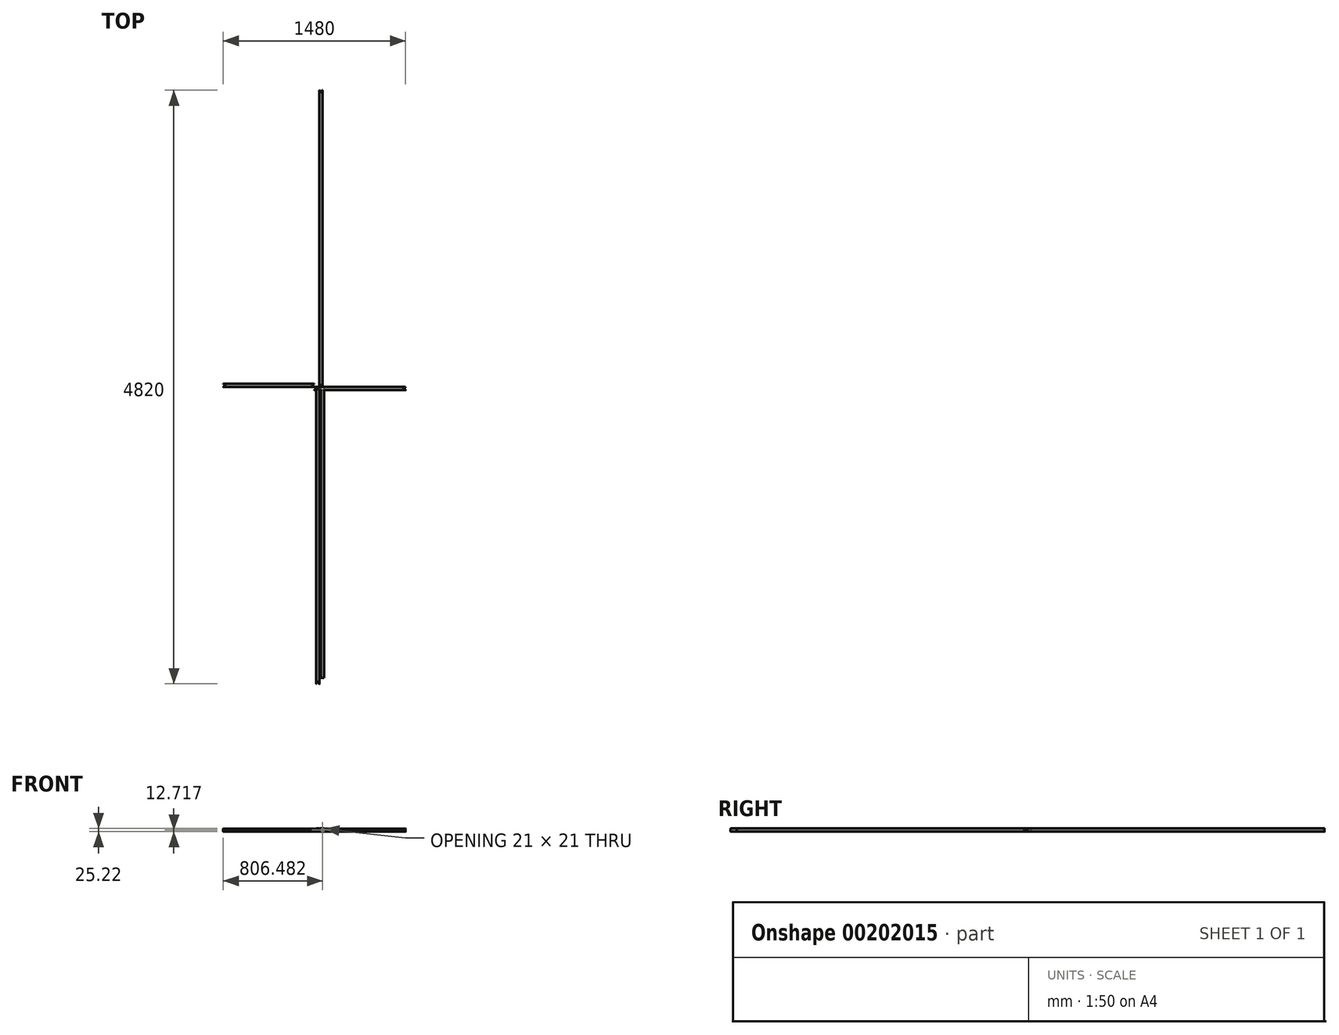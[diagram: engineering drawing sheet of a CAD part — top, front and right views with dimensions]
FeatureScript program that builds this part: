
annotation { "Feature Type Name" : "Feature", "Feature Type Description" : "" }
export const myFeature = defineFeature(function(context is Context, id is Id, definition is map)
    precondition{}
    {
        {
            var Q0;
            Q0=qCreatedBy(makeId("Front.planeOp"),FACE);
            var sketch = newSketch(context, id + "F0", { "sketchPlane" : qUnion([Q0])});
            skLineSegment(sketch, "E0.bottom", {"start": v(10, 12.5) * mm, "end": v(-10, 12.5) * mm});
            skLineSegment(sketch, "E0.top", {"start": v(10, -12.5) * mm, "end": v(-10, -12.5) * mm});
            skLineSegment(sketch, "E0.left", {"start": v(12.5, 10) * mm, "end": v(12.5, -10) * mm});
            skLineSegment(sketch, "E0.right", {"start": v(-12.5, 10) * mm, "end": v(-12.5, -10) * mm});
            skPoint(sketch, "E0.middle", {"position": v(0, 0) * mm});
            skLineSegment(sketch, "E1.0", {"start": v(8.5, 10.5) * mm, "end": v(-8.5, 10.5) * mm});
            skLineSegment(sketch, "E1.1", {"start": v(10.5, 8.5) * mm, "end": v(10.5, -8.5) * mm});
            skLineSegment(sketch, "E1.2", {"start": v(8.5, -10.5) * mm, "end": v(-8.5, -10.5) * mm});
            skLineSegment(sketch, "E1.3", {"start": v(-10.5, 8.5) * mm, "end": v(-10.5, -8.5) * mm});
            skPoint(sketch, "E2.visualSharp", {"position": v(-10.5, 10.5) * mm});
            skArc(sketch, "E2.filletArc", {"start": v(-8.5, 10.5) * mm, "mid": v(-9.91, 9.91) * mm, "end": v(-10.5, 8.5) * mm});
            skPoint(sketch, "E3.visualSharp", {"position": v(10.5, 10.5) * mm});
            skArc(sketch, "E3.filletArc", {"start": v(10.5, 8.5) * mm, "mid": v(9.91, 9.91) * mm, "end": v(8.5, 10.5) * mm});
            skPoint(sketch, "E4.visualSharp", {"position": v(10.5, -10.5) * mm});
            skArc(sketch, "E4.filletArc", {"start": v(8.5, -10.5) * mm, "mid": v(9.91, -9.91) * mm, "end": v(10.5, -8.5) * mm});
            skPoint(sketch, "E5.visualSharp", {"position": v(-10.5, -10.5) * mm});
            skArc(sketch, "E5.filletArc", {"start": v(-10.5, -8.5) * mm, "mid": v(-9.91, -9.91) * mm, "end": v(-8.5, -10.5) * mm});
            skPoint(sketch, "E6.visualSharp", {"position": v(12.5, 12.5) * mm});
            skArc(sketch, "E6.filletArc", {"start": v(12.5, 10) * mm, "mid": v(11.77, 11.77) * mm, "end": v(10, 12.5) * mm});
            skPoint(sketch, "E7.visualSharp", {"position": v(-12.5, 12.5) * mm});
            skArc(sketch, "E7.filletArc", {"start": v(-10, 12.5) * mm, "mid": v(-11.77, 11.77) * mm, "end": v(-12.5, 10) * mm});
            skPoint(sketch, "E8.visualSharp", {"position": v(12.5, -12.5) * mm});
            skArc(sketch, "E8.filletArc", {"start": v(10, -12.5) * mm, "mid": v(11.77, -11.77) * mm, "end": v(12.5, -10) * mm});
            skPoint(sketch, "E9.visualSharp", {"position": v(-12.5, -12.5) * mm});
            skArc(sketch, "E9.filletArc", {"start": v(-12.5, -10) * mm, "mid": v(-11.77, -11.77) * mm, "end": v(-10, -12.5) * mm});
            skSolve(sketch);
        }
        {
            var Q0;
            Q0=makeQuery(id+"F0.imprint","IMPRINT",FACE,{"disambiguationData":[TD([[makeQuery(id+"F0.imprint","IMPRINT",EDGE,{"derivedFrom":sQuery(id+"F0.wireOp",EDGE,"E0.bottom")}),1.0]])]});
            extrude(context, id + "F1", {"entities" : qUnion([Q0]), "depth" : 2410 * mm});
        }
        {
            var Q0;
            Q0=makeQuery(id+"F1.opExtrude","SWEPT_FACE",FACE,{"disambiguationData":[OSD([sQuery(id+"F0.wireOp",EDGE,"E0.bottom")])]});
            var sketch = newSketch(context, id + "F2", { "sketchPlane" : qUnion([Q0])});
            skLineSegment(sketch, "E10.0", {"start": v(-12.5, -2410) * mm, "end": v(-12.5, 0) * mm});
            skLineSegment(sketch, "E11.0", {"start": v(12.5, -2410) * mm, "end": v(12.5, 0) * mm});
            skLineSegment(sketch, "E12", {"start": v(-12.5, 0) * mm, "end": v(12.5, 0) * mm});
            skLineSegment(sketch, "E13", {"start": v(12.5, 0) * mm, "end": v(-12.5, -25) * mm});
            skLineSegment(sketch, "E14", {"start": v(-12.5, -25) * mm, "end": v(-12.5, 0) * mm});
            skLineSegment(sketch, "E15", {"start": v(12.5, -2410) * mm, "end": v(-12.5, -2385) * mm});
            skLineSegment(sketch, "E16", {"start": v(-12.5, -2385) * mm, "end": v(-12.5, -2410) * mm});
            skLineSegment(sketch, "E17", {"start": v(-12.5, -2410) * mm, "end": v(12.5, -2410) * mm});
            skSolve(sketch);
        }
        {
            var Q0;
            {var subQ0=sQuery(id+"F2.wireOp",EDGE,"E12");var subQ1=sQuery(id+"F0.wireOp",EDGE,"E0.bottom");var subQ2=makeQuery(id+"F1.opExtrude","SWEPT_EDGE",EDGE,{"disambiguationData":[OSD([subQ1,sQuery(id+"F0.wireOp",EDGE,"E6.filletArc")])]});var subQ3=makeQuery(id+"F2.imprint","INTERSECT",VERTEX,{"derivedFrom":[subQ2,subQ0]});var subQ4=makeQuery(id+"F1.opExtrude","SWEPT_EDGE",EDGE,{"disambiguationData":[OSD([subQ1,sQuery(id+"F0.wireOp",EDGE,"E7.filletArc")])]});var subQ5=makeQuery(id+"F2.imprint","INTERSECT",VERTEX,{"derivedFrom":[subQ4,subQ0]});Q0=makeQuery(id+"F2.imprint","IMPRINT",FACE,{"disambiguationData":[TD([[makeQuery(id+"F2.imprint","IMPRINT",EDGE,{"disambiguationData":[TD([[subQ3,-1.0],[subQ5,1.0]])],"derivedFrom":subQ0}),1.0]])]});}
            var Q1;
            {var subQ3=sQuery(id+"F2.wireOp",EDGE,"E14");Q1=makeQuery(id+"F2.imprint","IMPRINT",FACE,{"disambiguationData":[TD([[makeQuery(id+"F2.imprint","IMPRINT",EDGE,{"derivedFrom":subQ3}),-1.0]])]});}
            var Q2;
            {var subQ0=sQuery(id+"F2.wireOp",EDGE,"E12");var subQ1=makeQuery(id+"F1.opExtrude","SWEPT_EDGE",EDGE,{"disambiguationData":[OSD([sQuery(id+"F0.wireOp",EDGE,"E0.bottom"),sQuery(id+"F0.wireOp",EDGE,"E6.filletArc")])]});var subQ2=makeQuery(id+"F2.imprint","INTERSECT",VERTEX,{"derivedFrom":[subQ1,subQ0]});var subQ3=sQuery(id+"F2.wireOp",EDGE,"E13");var subQ4=makeQuery(id+"F2.imprint","INTERSECT",VERTEX,{"derivedFrom":[subQ0,subQ3]});Q2=makeQuery(id+"F2.imprint","IMPRINT",FACE,{"disambiguationData":[TD([[makeQuery(id+"F2.imprint","IMPRINT",EDGE,{"disambiguationData":[TD([[subQ2,-1.0],[subQ4,1.0]])],"derivedFrom":subQ0}),-1.0]])]});}
            var Q3;
            {var subQ0=sQuery(id+"F2.wireOp",EDGE,"E15");var subQ1=sQuery(id+"F0.wireOp",EDGE,"E0.bottom");var subQ2=makeQuery(id+"F1.opExtrude","SWEPT_EDGE",EDGE,{"disambiguationData":[OSD([subQ1,sQuery(id+"F0.wireOp",EDGE,"E6.filletArc")])]});var subQ3=makeQuery(id+"F2.imprint","INTERSECT",VERTEX,{"derivedFrom":[subQ2,subQ0]});Q3=makeQuery(id+"F2.imprint","IMPRINT",FACE,{"disambiguationData":[TD([[makeQuery(id+"F2.imprint","IMPRINT",EDGE,{"disambiguationData":[TD([[subQ3,-1.0]])],"derivedFrom":subQ0}),1.0]])]});}
            var Q4;
            {var subQ0=sQuery(id+"F2.wireOp",EDGE,"E16");Q4=makeQuery(id+"F2.imprint","IMPRINT",FACE,{"disambiguationData":[TD([[makeQuery(id+"F2.imprint","IMPRINT",EDGE,{"derivedFrom":subQ0}),1.0]])]});}
            var Q5;
            {var subQ0=sQuery(id+"F2.wireOp",EDGE,"E17");var subQ1=sQuery(id+"F2.wireOp",EDGE,"E15");var subQ2=makeQuery(id+"F2.imprint","INTERSECT",VERTEX,{"derivedFrom":[sQuery(id+"F2.wireOp",EDGE,"E11.0"),subQ1,subQ0]});Q5=makeQuery(id+"F2.imprint","IMPRINT",FACE,{"disambiguationData":[TD([[makeQuery(id+"F2.imprint","IMPRINT",EDGE,{"disambiguationData":[TD([[subQ2,-1.0]])],"derivedFrom":subQ1}),1.0]])]});}
            extrude(context, id + "F3", {"entities" : qUnion([Q0, Q1, Q2, Q3, Q4, Q5]), "operationType" : NewBodyOperationType.REMOVE, "endBound" : BoundingType.THROUGH_ALL, "oppositeDirection" : true, "depth" : 25 * mm});
        }
        {
            var Q0;
            Q0=qCreatedBy(makeId("Front.planeOp"),FACE);
            var sketch = newSketch(context, id + "F4", { "sketchPlane" : qUnion([Q0])});
            skLineSegment(sketch, "E18.bottom", {"start": v(-30.64, 12.45) * mm, "end": v(-50.64, 12.45) * mm});
            skLineSegment(sketch, "E18.top", {"start": v(-30.64, -12.55) * mm, "end": v(-50.64, -12.55) * mm});
            skLineSegment(sketch, "E18.left", {"start": v(-28.14, 9.95) * mm, "end": v(-28.14, -10.05) * mm});
            skLineSegment(sketch, "E18.right", {"start": v(-53.14, 9.95) * mm, "end": v(-53.14, -10.05) * mm});
            skPoint(sketch, "E18.middle", {"position": v(-40.64, -0.05) * mm});
            skLineSegment(sketch, "E19.0", {"start": v(-32.14, 10.45) * mm, "end": v(-49.14, 10.45) * mm});
            skLineSegment(sketch, "E19.1", {"start": v(-30.14, 8.45) * mm, "end": v(-30.14, -8.55) * mm});
            skLineSegment(sketch, "E19.2", {"start": v(-32.14, -10.55) * mm, "end": v(-49.14, -10.55) * mm});
            skLineSegment(sketch, "E19.3", {"start": v(-51.14, 8.45) * mm, "end": v(-51.14, -8.55) * mm});
            skPoint(sketch, "E20.visualSharp", {"position": v(-51.14, 10.45) * mm});
            skArc(sketch, "E20.filletArc", {"start": v(-49.14, 10.45) * mm, "mid": v(-50.56, 9.86) * mm, "end": v(-51.14, 8.45) * mm});
            skPoint(sketch, "E21.visualSharp", {"position": v(-30.14, 10.45) * mm});
            skArc(sketch, "E21.filletArc", {"start": v(-30.14, 8.45) * mm, "mid": v(-30.73, 9.86) * mm, "end": v(-32.14, 10.45) * mm});
            skPoint(sketch, "E22.visualSharp", {"position": v(-30.14, -10.55) * mm});
            skArc(sketch, "E22.filletArc", {"start": v(-32.14, -10.55) * mm, "mid": v(-30.73, -9.96) * mm, "end": v(-30.14, -8.55) * mm});
            skPoint(sketch, "E23.visualSharp", {"position": v(-51.14, -10.55) * mm});
            skArc(sketch, "E23.filletArc", {"start": v(-51.14, -8.55) * mm, "mid": v(-50.56, -9.96) * mm, "end": v(-49.14, -10.55) * mm});
            skPoint(sketch, "E24.visualSharp", {"position": v(-28.14, 12.45) * mm});
            skArc(sketch, "E24.filletArc", {"start": v(-28.14, 9.95) * mm, "mid": v(-28.87, 11.72) * mm, "end": v(-30.64, 12.45) * mm});
            skPoint(sketch, "E25.visualSharp", {"position": v(-53.14, 12.45) * mm});
            skArc(sketch, "E25.filletArc", {"start": v(-50.64, 12.45) * mm, "mid": v(-52.4, 11.72) * mm, "end": v(-53.14, 9.95) * mm});
            skPoint(sketch, "E26.visualSharp", {"position": v(-28.14, -12.55) * mm});
            skArc(sketch, "E26.filletArc", {"start": v(-30.64, -12.55) * mm, "mid": v(-28.87, -11.82) * mm, "end": v(-28.14, -10.05) * mm});
            skPoint(sketch, "E27.visualSharp", {"position": v(-53.14, -12.55) * mm});
            skArc(sketch, "E27.filletArc", {"start": v(-53.14, -10.05) * mm, "mid": v(-52.4, -11.82) * mm, "end": v(-50.64, -12.55) * mm});
            skSolve(sketch);
        }
        {
            var Q0;
            Q0=makeQuery(id+"F4.imprint","IMPRINT",FACE,{"disambiguationData":[TD([[makeQuery(id+"F4.imprint","IMPRINT",EDGE,{"derivedFrom":sQuery(id+"F4.wireOp",EDGE,"E18.bottom")}),1.0]])]});
            extrude(context, id + "F5", {"entities" : qUnion([Q0]), "depth" : 740 * mm});
        }
        {
            var Q0;
            Q0=makeQuery(id+"F5.opExtrude","SWEPT_FACE",FACE,{"disambiguationData":[OSD([sQuery(id+"F4.wireOp",EDGE,"E18.bottom")])]});
            var sketch = newSketch(context, id + "F6", { "sketchPlane" : qUnion([Q0])});
            skLineSegment(sketch, "E28.0", {"start": v(-28.14, -740) * mm, "end": v(-28.14, 0) * mm});
            skLineSegment(sketch, "E29.0", {"start": v(-53.14, -740) * mm, "end": v(-53.14, 0) * mm});
            skLineSegment(sketch, "E30", {"start": v(-53.14, 0) * mm, "end": v(-28.14, 0) * mm});
            skLineSegment(sketch, "E31", {"start": v(-28.14, 0) * mm, "end": v(-53.14, -25) * mm});
            skLineSegment(sketch, "E32", {"start": v(-53.14, -25) * mm, "end": v(-53.14, 0) * mm});
            skLineSegment(sketch, "E33", {"start": v(-28.14, -740) * mm, "end": v(-53.14, -715) * mm});
            skLineSegment(sketch, "E34", {"start": v(-53.14, -715) * mm, "end": v(-53.14, -740) * mm});
            skLineSegment(sketch, "E35", {"start": v(-53.14, -740) * mm, "end": v(-28.14, -740) * mm});
            skSolve(sketch);
        }
        {
            var Q0;
            {var subQ0=sQuery(id+"F6.wireOp",EDGE,"E34");Q0=makeQuery(id+"F6.imprint","IMPRINT",FACE,{"disambiguationData":[TD([[makeQuery(id+"F6.imprint","IMPRINT",EDGE,{"derivedFrom":subQ0}),1.0]])]});}
            var Q1;
            {var subQ0=sQuery(id+"F6.wireOp",EDGE,"E33");var subQ1=sQuery(id+"F4.wireOp",EDGE,"E18.bottom");var subQ2=makeQuery(id+"F5.opExtrude","SWEPT_EDGE",EDGE,{"disambiguationData":[OSD([subQ1,sQuery(id+"F4.wireOp",EDGE,"E24.filletArc")])]});var subQ3=makeQuery(id+"F6.imprint","INTERSECT",VERTEX,{"derivedFrom":[subQ2,subQ0]});Q1=makeQuery(id+"F6.imprint","IMPRINT",FACE,{"disambiguationData":[TD([[makeQuery(id+"F6.imprint","IMPRINT",EDGE,{"disambiguationData":[TD([[subQ3,-1.0]])],"derivedFrom":subQ0}),1.0]])]});}
            var Q2;
            {var subQ0=sQuery(id+"F6.wireOp",EDGE,"E35");var subQ1=sQuery(id+"F6.wireOp",EDGE,"E33");var subQ2=makeQuery(id+"F6.imprint","INTERSECT",VERTEX,{"derivedFrom":[sQuery(id+"F6.wireOp",EDGE,"E28.0"),subQ1,subQ0]});Q2=makeQuery(id+"F6.imprint","IMPRINT",FACE,{"disambiguationData":[TD([[makeQuery(id+"F6.imprint","IMPRINT",EDGE,{"disambiguationData":[TD([[subQ2,-1.0]])],"derivedFrom":subQ1}),1.0]])]});}
            var Q3;
            {var subQ3=sQuery(id+"F6.wireOp",EDGE,"E32");Q3=makeQuery(id+"F6.imprint","IMPRINT",FACE,{"disambiguationData":[TD([[makeQuery(id+"F6.imprint","IMPRINT",EDGE,{"derivedFrom":subQ3}),-1.0]])]});}
            var Q4;
            {var subQ0=sQuery(id+"F6.wireOp",EDGE,"E30");var subQ1=sQuery(id+"F4.wireOp",EDGE,"E18.bottom");var subQ2=makeQuery(id+"F5.opExtrude","SWEPT_EDGE",EDGE,{"disambiguationData":[OSD([subQ1,sQuery(id+"F4.wireOp",EDGE,"E24.filletArc")])]});var subQ3=makeQuery(id+"F6.imprint","INTERSECT",VERTEX,{"derivedFrom":[subQ2,subQ0]});var subQ4=makeQuery(id+"F5.opExtrude","SWEPT_EDGE",EDGE,{"disambiguationData":[OSD([subQ1,sQuery(id+"F4.wireOp",EDGE,"E25.filletArc")])]});var subQ5=makeQuery(id+"F6.imprint","INTERSECT",VERTEX,{"derivedFrom":[subQ4,subQ0]});Q4=makeQuery(id+"F6.imprint","IMPRINT",FACE,{"disambiguationData":[TD([[makeQuery(id+"F6.imprint","IMPRINT",EDGE,{"disambiguationData":[TD([[subQ3,-1.0],[subQ5,1.0]])],"derivedFrom":subQ0}),1.0]])]});}
            var Q5;
            {var subQ0=sQuery(id+"F6.wireOp",EDGE,"E30");var subQ1=makeQuery(id+"F5.opExtrude","SWEPT_EDGE",EDGE,{"disambiguationData":[OSD([sQuery(id+"F4.wireOp",EDGE,"E18.bottom"),sQuery(id+"F4.wireOp",EDGE,"E24.filletArc")])]});var subQ2=makeQuery(id+"F6.imprint","INTERSECT",VERTEX,{"derivedFrom":[subQ1,subQ0]});var subQ3=sQuery(id+"F6.wireOp",EDGE,"E31");var subQ4=makeQuery(id+"F6.imprint","INTERSECT",VERTEX,{"derivedFrom":[sQuery(id+"F6.wireOp",EDGE,"E28.0"),subQ0,subQ3]});Q5=makeQuery(id+"F6.imprint","IMPRINT",FACE,{"disambiguationData":[TD([[makeQuery(id+"F6.imprint","IMPRINT",EDGE,{"disambiguationData":[TD([[subQ2,-1.0],[subQ4,1.0]])],"derivedFrom":subQ0}),-1.0]])]});}
            extrude(context, id + "F7", {"entities" : qUnion([Q0, Q1, Q2, Q3, Q4, Q5]), "operationType" : NewBodyOperationType.REMOVE, "oppositeDirection" : true, "depth" : 25 * mm});
        }
        {
            var Q0;
            Q0=qCreatedBy(makeId("Front.planeOp"),FACE);
            var sketch = newSketch(context, id + "F8", { "sketchPlane" : qUnion([Q0])});
            skLineSegment(sketch, "E36.bottom", {"start": v(48.34, 12.67) * mm, "end": v(28.34, 12.67) * mm});
            skLineSegment(sketch, "E36.top", {"start": v(48.34, -12.33) * mm, "end": v(28.34, -12.33) * mm});
            skLineSegment(sketch, "E36.left", {"start": v(50.84, 10.17) * mm, "end": v(50.84, -9.83) * mm});
            skLineSegment(sketch, "E36.right", {"start": v(25.84, 10.17) * mm, "end": v(25.84, -9.83) * mm});
            skPoint(sketch, "E36.middle", {"position": v(38.34, 0.17) * mm});
            skLineSegment(sketch, "E37.0", {"start": v(46.84, 10.67) * mm, "end": v(29.84, 10.67) * mm});
            skLineSegment(sketch, "E37.1", {"start": v(48.84, 8.67) * mm, "end": v(48.84, -8.33) * mm});
            skLineSegment(sketch, "E37.2", {"start": v(46.84, -10.33) * mm, "end": v(29.84, -10.33) * mm});
            skLineSegment(sketch, "E37.3", {"start": v(27.84, 8.67) * mm, "end": v(27.84, -8.33) * mm});
            skPoint(sketch, "E38.visualSharp", {"position": v(27.84, 10.67) * mm});
            skArc(sketch, "E38.filletArc", {"start": v(29.84, 10.67) * mm, "mid": v(28.43, 10.08) * mm, "end": v(27.84, 8.67) * mm});
            skPoint(sketch, "E39.visualSharp", {"position": v(48.84, 10.67) * mm});
            skArc(sketch, "E39.filletArc", {"start": v(48.84, 8.67) * mm, "mid": v(48.26, 10.08) * mm, "end": v(46.84, 10.67) * mm});
            skPoint(sketch, "E40.visualSharp", {"position": v(48.84, -10.33) * mm});
            skArc(sketch, "E40.filletArc", {"start": v(46.84, -10.33) * mm, "mid": v(48.26, -9.75) * mm, "end": v(48.84, -8.33) * mm});
            skPoint(sketch, "E41.visualSharp", {"position": v(27.84, -10.33) * mm});
            skArc(sketch, "E41.filletArc", {"start": v(27.84, -8.33) * mm, "mid": v(28.43, -9.75) * mm, "end": v(29.84, -10.33) * mm});
            skPoint(sketch, "E42.visualSharp", {"position": v(50.84, 12.67) * mm});
            skArc(sketch, "E42.filletArc", {"start": v(50.84, 10.17) * mm, "mid": v(50.1, 11.93) * mm, "end": v(48.34, 12.67) * mm});
            skPoint(sketch, "E43.visualSharp", {"position": v(25.84, 12.67) * mm});
            skArc(sketch, "E43.filletArc", {"start": v(28.34, 12.67) * mm, "mid": v(26.57, 11.93) * mm, "end": v(25.84, 10.17) * mm});
            skPoint(sketch, "E44.visualSharp", {"position": v(50.84, -12.33) * mm});
            skArc(sketch, "E44.filletArc", {"start": v(48.34, -12.33) * mm, "mid": v(50.1, -11.6) * mm, "end": v(50.84, -9.83) * mm});
            skPoint(sketch, "E45.visualSharp", {"position": v(25.84, -12.33) * mm});
            skArc(sketch, "E45.filletArc", {"start": v(25.84, -9.83) * mm, "mid": v(26.57, -11.6) * mm, "end": v(28.34, -12.33) * mm});
            skSolve(sketch);
        }
        {
            var Q0;
            Q0=makeQuery(id+"F8.imprint","IMPRINT",FACE,{"disambiguationData":[TD([[makeQuery(id+"F8.imprint","IMPRINT",EDGE,{"derivedFrom":sQuery(id+"F8.wireOp",EDGE,"E36.bottom")}),1.0]])]});
            extrude(context, id + "F9", {"entities" : qUnion([Q0]), "depth" : 2360 * mm});
        }
        {
            var Q0;
            Q0=makeQuery(id+"F1.opExtrude","SWEPT_BODY",BODY,{"disambiguationData":[OSD([sQuery(id+"F0.wireOp",EDGE,"E0.bottom"),sQuery(id+"F0.wireOp",EDGE,"E0.top"),sQuery(id+"F0.wireOp",EDGE,"E0.left"),sQuery(id+"F0.wireOp",EDGE,"E0.right"),sQuery(id+"F0.wireOp",EDGE,"E1.0"),sQuery(id+"F0.wireOp",EDGE,"E1.1"),sQuery(id+"F0.wireOp",EDGE,"E1.2"),sQuery(id+"F0.wireOp",EDGE,"E1.3"),sQuery(id+"F0.wireOp",EDGE,"E2.filletArc"),sQuery(id+"F0.wireOp",EDGE,"E3.filletArc"),sQuery(id+"F0.wireOp",EDGE,"E4.filletArc"),sQuery(id+"F0.wireOp",EDGE,"E5.filletArc"),sQuery(id+"F0.wireOp",EDGE,"E6.filletArc"),sQuery(id+"F0.wireOp",EDGE,"E7.filletArc"),sQuery(id+"F0.wireOp",EDGE,"E8.filletArc"),sQuery(id+"F0.wireOp",EDGE,"E9.filletArc")])]});
            var Q1;
            Q1=makeQuery(id+"F3.boolean.opBoolean","MERGE",EDGE,{"derivedFrom":[makeQuery(id+"F1.opExtrude","CAP_EDGE",EDGE,{"disambiguationData":[OSD([sQuery(id+"F0.wireOp",EDGE,"E0.left")])],"isStart":true}),makeQuery(id+"F3.opExtrude","SWEPT_EDGE",EDGE,{"disambiguationData":[OSD([sQuery(id+"F2.wireOp",EDGE,"E11.0"),sQuery(id+"F2.wireOp",EDGE,"E12"),sQuery(id+"F2.wireOp",EDGE,"E13")])]})]});
            transform(context, id + "F10", {"entities" : qUnion([Q0]), "transformType" : TransformType.ROTATION, "transformAxis" : qUnion([Q1]), "angle" : 180 * degree, "makeCopy" : true});
        }
        {
            var Q0;
            Q0=makeQuery(id+"F5.opExtrude","SWEPT_BODY",BODY,{"disambiguationData":[OSD([sQuery(id+"F4.wireOp",EDGE,"E18.bottom"),sQuery(id+"F4.wireOp",EDGE,"E18.top"),sQuery(id+"F4.wireOp",EDGE,"E18.left"),sQuery(id+"F4.wireOp",EDGE,"E18.right"),sQuery(id+"F4.wireOp",EDGE,"E19.0"),sQuery(id+"F4.wireOp",EDGE,"E19.1"),sQuery(id+"F4.wireOp",EDGE,"E19.2"),sQuery(id+"F4.wireOp",EDGE,"E19.3"),sQuery(id+"F4.wireOp",EDGE,"E20.filletArc"),sQuery(id+"F4.wireOp",EDGE,"E21.filletArc"),sQuery(id+"F4.wireOp",EDGE,"E22.filletArc"),sQuery(id+"F4.wireOp",EDGE,"E23.filletArc"),sQuery(id+"F4.wireOp",EDGE,"E24.filletArc"),sQuery(id+"F4.wireOp",EDGE,"E25.filletArc"),sQuery(id+"F4.wireOp",EDGE,"E26.filletArc"),sQuery(id+"F4.wireOp",EDGE,"E27.filletArc")])]});
            var Q1;
            Q1=makeQuery(id+"F7.boolean.opBoolean","MERGE",EDGE,{"derivedFrom":[makeQuery(id+"F5.opExtrude","CAP_EDGE",EDGE,{"disambiguationData":[OSD([sQuery(id+"F4.wireOp",EDGE,"E18.left")])],"isStart":true}),makeQuery(id+"F7.opExtrude","SWEPT_EDGE",EDGE,{"disambiguationData":[OSD([sQuery(id+"F6.wireOp",EDGE,"E28.0"),sQuery(id+"F6.wireOp",EDGE,"E30"),sQuery(id+"F6.wireOp",EDGE,"E31")])]})]});
            transform(context, id + "F11", {"entities" : qUnion([Q0]), "transformType" : TransformType.ROTATION, "transformAxis" : qUnion([Q1]), "angle" : 90 * degree, "makeCopy" : false});
        }
        {
            var Q0;
            Q0=makeQuery(id+"F5.opExtrude","SWEPT_BODY",BODY,{"disambiguationData":[OSD([sQuery(id+"F4.wireOp",EDGE,"E18.bottom"),sQuery(id+"F4.wireOp",EDGE,"E18.top"),sQuery(id+"F4.wireOp",EDGE,"E18.left"),sQuery(id+"F4.wireOp",EDGE,"E18.right"),sQuery(id+"F4.wireOp",EDGE,"E19.0"),sQuery(id+"F4.wireOp",EDGE,"E19.1"),sQuery(id+"F4.wireOp",EDGE,"E19.2"),sQuery(id+"F4.wireOp",EDGE,"E19.3"),sQuery(id+"F4.wireOp",EDGE,"E20.filletArc"),sQuery(id+"F4.wireOp",EDGE,"E21.filletArc"),sQuery(id+"F4.wireOp",EDGE,"E22.filletArc"),sQuery(id+"F4.wireOp",EDGE,"E23.filletArc"),sQuery(id+"F4.wireOp",EDGE,"E24.filletArc"),sQuery(id+"F4.wireOp",EDGE,"E25.filletArc"),sQuery(id+"F4.wireOp",EDGE,"E26.filletArc"),sQuery(id+"F4.wireOp",EDGE,"E27.filletArc")])]});
            var Q1;
            Q1=makeQuery(id+"F7.boolean.opBoolean","MERGE",EDGE,{"derivedFrom":[makeQuery(id+"F5.opExtrude","CAP_EDGE",EDGE,{"disambiguationData":[OSD([sQuery(id+"F4.wireOp",EDGE,"E18.left")])],"isStart":true}),makeQuery(id+"F7.opExtrude","SWEPT_EDGE",EDGE,{"disambiguationData":[OSD([sQuery(id+"F6.wireOp",EDGE,"E28.0"),sQuery(id+"F6.wireOp",EDGE,"E30"),sQuery(id+"F6.wireOp",EDGE,"E31")])]})]});
            transform(context, id + "F12", {"entities" : qUnion([Q0]), "transformType" : TransformType.ROTATION, "transformAxis" : qUnion([Q1]), "angle" : 180 * degree, "makeCopy" : true});
        }
    });
